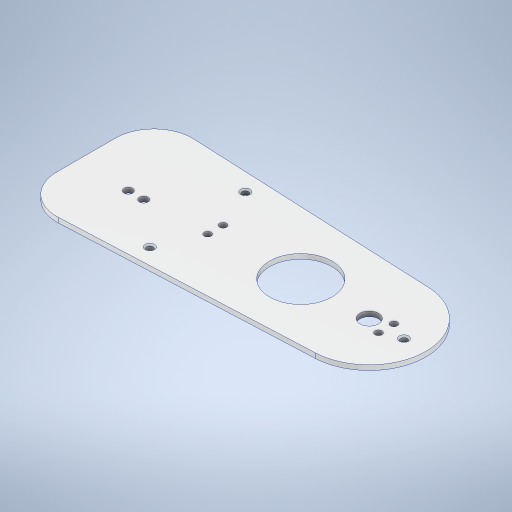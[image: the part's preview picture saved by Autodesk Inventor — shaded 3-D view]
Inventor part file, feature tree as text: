
AUTODESK INVENTOR PART (.ipt)
format: ipt  version: 2023 (Build 270158000, 158)  size: 301,056 bytes
history: native  units: in
note: dims shown in document units (in); Inventor stores cm internally (conversion verified against a paired STEP export)
features: extrude x3, sketch x3, hole x1
ambient origin geometry x8: Origin, YZ Plane, XZ Plane, XY Plane, X Axis, Y Axis, Z Axis, Center Point
bodies: Solid1 (feature_tree)
feature tree (7):
  extrude  "Main"  Depth=6.2598in
  extrude  "Axis Holes"  Depth=1.45in
  extrude  "Extrusion6"  Depth=0.3937in
  hole  "Hole1"  [1 undecoded]
  sketch  "Sketch1"  dims[d0=1.9685in d1=6.2598in]
  sketch  "Sketch5"  dims[d2=1.5in d3=1.45in]
  sketch  "Sketch9"  dims[d4=0.125in d5=0.0in d6=1.5945in d7=0.0in d8=0.0in d40=0.4724in d41=1.751in d43=2.0in d44=0.2756in d45=0.3937in d46=0.2165in d47=0.0in d48=0.0in d66=0.1628in d67=0.3937in d68=0.2362in d69=0.0787in d70=90.0deg d71=0.315in d72=0.8108in d73=2.6401in d74=2.6401in d75=1.2205in d76=1.2205in d77=3.7402in d78=0.315in d79=0.1969in d80=0.3937in d81=0.315in d82=0.1969in d83=0.3937in d84=0.1772in d85=0.1772in d86=0.1772in d87=0.1772in]
note: 1 required parameter value undecoded (feature->parameter linkage not recoverable at this tier; creation-order binding heuristic only, values carry confidence <= 0.55)
